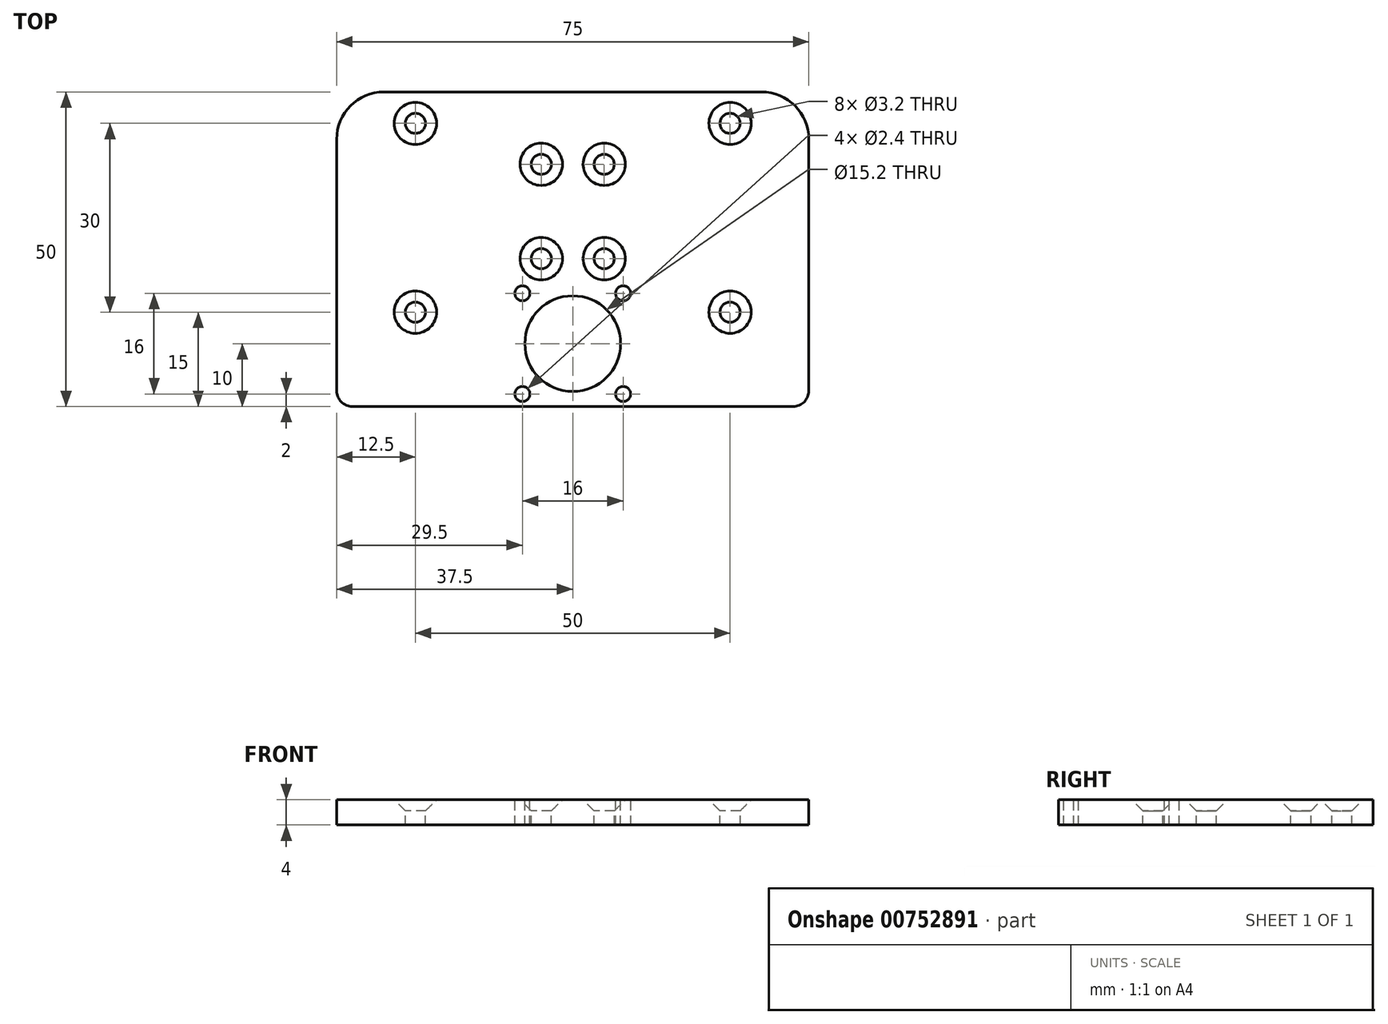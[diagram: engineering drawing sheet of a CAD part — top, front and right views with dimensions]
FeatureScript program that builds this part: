
annotation { "Feature Type Name" : "Feature", "Feature Type Description" : "" }
export const myFeature = defineFeature(function(context is Context, id is Id, definition is map)
    precondition{}
    {
        {
            var Q0;
            Q0=qCreatedBy(makeId("Top.planeOp"),FACE);
            var sketch = newSketch(context, id + "F0", { "sketchPlane" : qUnion([Q0])});
            skLineSegment(sketch, "E0.bottom", {"start": v(-10, 10) * mm, "end": v(10, 10) * mm, "construction": true});
            skLineSegment(sketch, "E0.top", {"start": v(-10, -10) * mm, "end": v(10, -10) * mm, "construction": true});
            skLineSegment(sketch, "E0.left", {"start": v(-10, 10) * mm, "end": v(-10, -10) * mm, "construction": true});
            skLineSegment(sketch, "E0.right", {"start": v(10, 10) * mm, "end": v(10, -10) * mm, "construction": true});
            skPoint(sketch, "E0.middle", {"position": v(0, 0) * mm});
            skLineSegment(sketch, "E1.bottom", {"start": v(-8, 8) * mm, "end": v(8, 8) * mm, "construction": true});
            skLineSegment(sketch, "E1.top", {"start": v(-8, -8) * mm, "end": v(8, -8) * mm, "construction": true});
            skLineSegment(sketch, "E1.left", {"start": v(-8, 8) * mm, "end": v(-8, -8) * mm, "construction": true});
            skLineSegment(sketch, "E1.right", {"start": v(8, 8) * mm, "end": v(8, -8) * mm, "construction": true});
            skPoint(sketch, "E2", {"position": v(-8, 8) * mm});
            skPoint(sketch, "E3", {"position": v(8, 8) * mm});
            skPoint(sketch, "E4", {"position": v(8, -8) * mm});
            skPoint(sketch, "E5", {"position": v(-8, -8) * mm});
            skCircle(sketch, "E6", {"center": v(0, 0) * mm, "radius": 7.6 * mm});
            skLineSegment(sketch, "E7.bottom", {"start": v(-20, 0) * mm, "end": v(-30, 0) * mm, "construction": true});
            skLineSegment(sketch, "E7.top", {"start": v(-20, 10) * mm, "end": v(-30, 10) * mm, "construction": true});
            skLineSegment(sketch, "E7.left", {"start": v(-20, 0) * mm, "end": v(-20, 10) * mm, "construction": true});
            skLineSegment(sketch, "E7.right", {"start": v(-30, 0) * mm, "end": v(-30, 10) * mm, "construction": true});
            skPoint(sketch, "E7.middle", {"position": v(-25, 5) * mm});
            skLineSegment(sketch, "E8.bottom", {"start": v(-20, -6.5) * mm, "end": v(-30, -6.5) * mm, "construction": true});
            skLineSegment(sketch, "E8.left", {"start": v(-20, -6.5) * mm, "end": v(-20, 0) * mm, "construction": true});
            skLineSegment(sketch, "E8.right", {"start": v(-30, -6.5) * mm, "end": v(-30, 0) * mm, "construction": true});
            skLineSegment(sketch, "E9.bottom", {"start": v(-35, -2) * mm, "end": v(-30, -2) * mm, "construction": true});
            skLineSegment(sketch, "E9.top", {"start": v(-35, -10) * mm, "end": v(-15, -10) * mm, "construction": true});
            skLineSegment(sketch, "E9.left", {"start": v(-35, -2) * mm, "end": v(-35, -10) * mm, "construction": true});
            skLineSegment(sketch, "E9.right", {"start": v(-15, -2) * mm, "end": v(-15, -10) * mm, "construction": true});
            skCircle(sketch, "E10.0", {"center": v(0, 0) * mm, "radius": 3 * mm, "construction": true});
            skLineSegment(sketch, "E11.MirrorCS", {"start": v(20, 10) * mm, "end": v(30, 10) * mm, "construction": true});
            skLineSegment(sketch, "E12.MirrorCS", {"start": v(30, 0) * mm, "end": v(30, 10) * mm, "construction": true});
            skLineSegment(sketch, "E13.MirrorCS", {"start": v(20, 0) * mm, "end": v(20, 10) * mm, "construction": true});
            skPoint(sketch, "E14.MirrorP", {"position": v(25, 5) * mm});
            skLineSegment(sketch, "E15.MirrorCS", {"start": v(20, 0) * mm, "end": v(30, 0) * mm, "construction": true});
            skLineSegment(sketch, "E16.MirrorCS", {"start": v(30, -6.5) * mm, "end": v(30, 0) * mm, "construction": true});
            skLineSegment(sketch, "E17.MirrorCS", {"start": v(20, -6.5) * mm, "end": v(20, 0) * mm, "construction": true});
            skLineSegment(sketch, "E18.MirrorCS", {"start": v(35, -2) * mm, "end": v(15, -2) * mm, "construction": true});
            skLineSegment(sketch, "E19.MirrorCS", {"start": v(35, -2) * mm, "end": v(35, -10) * mm, "construction": true});
            skLineSegment(sketch, "E20.MirrorCS", {"start": v(15, -2) * mm, "end": v(15, -10) * mm, "construction": true});
            skLineSegment(sketch, "E21.MirrorCS", {"start": v(20, -6.5) * mm, "end": v(30, -6.5) * mm, "construction": true});
            skLineSegment(sketch, "E22.MirrorCS", {"start": v(35, -10) * mm, "end": v(15, -10) * mm, "construction": true});
            skLineSegment(sketch, "E23.trimOffspring", {"start": v(-20, -2) * mm, "end": v(-15, -2) * mm, "construction": true});
            skLineSegment(sketch, "E24.bottom", {"start": v(-37.5, 40) * mm, "end": v(37.5, 40) * mm});
            skLineSegment(sketch, "E24.top", {"start": v(-37.5, -10) * mm, "end": v(37.5, -10) * mm});
            skLineSegment(sketch, "E24.right", {"start": v(37.5, 40) * mm, "end": v(37.5, -10) * mm});
            skLineSegment(sketch, "E25.bottom", {"start": v(-14.45, 31) * mm, "end": v(14.45, 31) * mm, "construction": true});
            skLineSegment(sketch, "E25.top", {"start": v(-14.45, 11) * mm, "end": v(14.45, 11) * mm, "construction": true});
            skLineSegment(sketch, "E25.left", {"start": v(-14.45, 31) * mm, "end": v(-14.45, 11) * mm, "construction": true});
            skLineSegment(sketch, "E25.right", {"start": v(14.45, 31) * mm, "end": v(14.45, 11) * mm, "construction": true});
            skPoint(sketch, "E25.middle", {"position": v(0, 21) * mm});
            skLineSegment(sketch, "E26.bottom", {"start": v(-5, 28.5) * mm, "end": v(5, 28.5) * mm, "construction": true});
            skLineSegment(sketch, "E26.top", {"start": v(-5, 13.5) * mm, "end": v(5, 13.5) * mm, "construction": true});
            skLineSegment(sketch, "E26.left", {"start": v(-5, 28.5) * mm, "end": v(-5, 13.5) * mm, "construction": true});
            skLineSegment(sketch, "E26.right", {"start": v(5, 28.5) * mm, "end": v(5, 13.5) * mm, "construction": true});
            skLineSegment(sketch, "E27.bottom", {"start": v(37.5, 26) * mm, "end": v(-37.5, 26) * mm, "construction": true});
            skLineSegment(sketch, "E27.top", {"start": v(37.5, 16) * mm, "end": v(-37.5, 16) * mm, "construction": true});
            skLineSegment(sketch, "E27.left", {"start": v(37.5, 26) * mm, "end": v(37.5, 16) * mm, "construction": true});
            skLineSegment(sketch, "E27.right", {"start": v(-37.5, 26) * mm, "end": v(-37.5, 16) * mm, "construction": true});
            skLineSegment(sketch, "E28", {"start": v(-37.5, 21) * mm, "end": v(37.5, 21) * mm, "construction": true});
            skLineSegment(sketch, "E29", {"start": v(-37.5, 40) * mm, "end": v(-37.5, -10) * mm});
            skLineSegment(sketch, "E30.bottom", {"start": v(12.5, 5) * mm, "end": v(-12.5, 5) * mm, "construction": true});
            skLineSegment(sketch, "E30.top", {"start": v(12.5, -5) * mm, "end": v(-12.5, -5) * mm, "construction": true});
            skLineSegment(sketch, "E30.left", {"start": v(12.5, 5) * mm, "end": v(12.5, -5) * mm, "construction": true});
            skLineSegment(sketch, "E30.right", {"start": v(-12.5, 5) * mm, "end": v(-12.5, -5) * mm, "construction": true});
            skLineSegment(sketch, "E31.bottom", {"start": v(-30, 40) * mm, "end": v(-20, 40) * mm, "construction": true});
            skLineSegment(sketch, "E31.top", {"start": v(-30, 30) * mm, "end": v(-20, 30) * mm, "construction": true});
            skLineSegment(sketch, "E31.left", {"start": v(-30, 40) * mm, "end": v(-30, 30) * mm, "construction": true});
            skLineSegment(sketch, "E31.right", {"start": v(-20, 40) * mm, "end": v(-20, 30) * mm, "construction": true});
            skPoint(sketch, "E31.middle", {"position": v(-25, 35) * mm});
            skLineSegment(sketch, "E32.MirrorCS", {"start": v(20, 40) * mm, "end": v(20, 30) * mm, "construction": true});
            skLineSegment(sketch, "E33.MirrorCS", {"start": v(30, 40) * mm, "end": v(20, 40) * mm, "construction": true});
            skLineSegment(sketch, "E34.MirrorCS", {"start": v(30, 40) * mm, "end": v(30, 30) * mm, "construction": true});
            skLineSegment(sketch, "E35.MirrorCS", {"start": v(30, 30) * mm, "end": v(20, 30) * mm, "construction": true});
            skPoint(sketch, "E36.MirrorP", {"position": v(25, 35) * mm});
            skCircle(sketch, "E37", {"center": v(-5, 13.5) * mm, "radius": 3 * mm, "construction": true});
            skSolve(sketch);
        }
        {
            var Q0;
            Q0=makeQuery(id+"F0.imprint","IMPRINT",FACE,{"disambiguationData":[TD([[makeQuery(id+"F0.imprint","IMPRINT",EDGE,{"derivedFrom":sQuery(id+"F0.wireOp",EDGE,"E6")}),-1.0]])]});
            extrude(context, id + "F1", {"entities" : qUnion([Q0]), "oppositeDirection" : true, "depth" : 4 * mm, "offsetDistance" : 25 * mm});
        }
        {
            var Q0;
            Q0=sQuery(id+"F0.wireOp",VERTEX,"E2");
            var Q1;
            Q1=sQuery(id+"F0.wireOp",VERTEX,"E3");
            var Q2;
            Q2=sQuery(id+"F0.wireOp",VERTEX,"E4");
            var Q3;
            Q3=sQuery(id+"F0.wireOp",VERTEX,"E5");
            var Q4;
            Q4=makeQuery(id+"F1.opExtrude","SWEPT_BODY",BODY,{"disambiguationData":[OSD([sQuery(id+"F0.wireOp",EDGE,"E6"),sQuery(id+"F0.wireOp",EDGE,"E24.bottom"),sQuery(id+"F0.wireOp",EDGE,"E24.top"),sQuery(id+"F0.wireOp",EDGE,"E24.left"),sQuery(id+"F0.wireOp",EDGE,"E24.right")])]});
            hole(context, id + "F2", {"style" : HoleStyle.SIMPLE, "endStyle" : HoleEndStyle.THROUGH, "standardTappedOrClearance" : lookupTablePath({ "fit" : "Normal", "standard" : "ISO", "size" : "M2", "type" : "Clearance" }), "standardBlindInLast" : lookupTablePath({ "fit" : "Normal", "standard" : "ISO", "engagement" : "75%", "pitch" : "0.25 mm", "size" : "M2", "type" : "Clearance & tapped" }), "holeDiameter" : 2.4 * mm, "majorDiameter" : 2 * mm, "isTappedThrough" : true, "tappedDepth" : 3 * mm, "tapClearance" : 3, "startFromSketch" : true, "locations" : qUnion([Q0, Q1, Q2, Q3]), "scope" : qUnion([Q4])});
        }
        {
            var Q0;
            Q0=sQuery(id+"F0.wireOp",VERTEX,"E7.middle");
            var Q1;
            Q1=sQuery(id+"F0.wireOp",VERTEX,"E14.MirrorP");
            var Q2;
            Q2=sQuery(id+"F0.wireOp",VERTEX,"379273be-aec1-4a05-9cb9-dedefb76e79c0.MirrorP");
            var Q3;
            Q3=sQuery(id+"F0.wireOp",VERTEX,"66311432-f337-42e8-b5ac-b30e00d571a50.MirrorP");
            var Q4;
            Q4=sQuery(id+"F0.wireOp",VERTEX,"E26.bottom.start");
            var Q5;
            Q5=sQuery(id+"F0.wireOp",VERTEX,"E26.bottom.end");
            var Q6;
            Q6=sQuery(id+"F0.wireOp",VERTEX,"E26.top.end");
            var Q7;
            Q7=sQuery(id+"F0.wireOp",VERTEX,"E26.top.start");
            var Q8;
            Q8=sQuery(id+"F0.wireOp",VERTEX,"E31.middle");
            var Q9;
            Q9=sQuery(id+"F0.wireOp",VERTEX,"E36.MirrorP");
            var Q10;
            Q10=makeQuery(id+"F1.opExtrude","SWEPT_BODY",BODY,{"disambiguationData":[OSD([sQuery(id+"F0.wireOp",EDGE,"E6"),sQuery(id+"F0.wireOp",EDGE,"E24.bottom"),sQuery(id+"F0.wireOp",EDGE,"E24.top"),sQuery(id+"F0.wireOp",EDGE,"E24.left"),sQuery(id+"F0.wireOp",EDGE,"E24.right")])]});
            hole(context, id + "F3", {"style" : HoleStyle.C_SINK, "endStyle" : HoleEndStyle.THROUGH, "standardTappedOrClearance" : lookupTablePath({ "fit" : "Close", "standard" : "ISO", "size" : "M3", "type" : "Clearance" }), "standardBlindInLast" : lookupTablePath({ "fit" : "Close", "standard" : "ISO", "engagement" : "75%", "pitch" : "0.5 mm", "size" : "M3", "type" : "Clearance & tapped" }), "holeDiameter" : 3.2 * mm, "cSinkDiameter" : 6.72 * mm, "cSinkAngle" : 90 * degree, "majorDiameter" : 5 * mm, "isTappedThrough" : true, "tappedDepth" : 3 * mm, "tapClearance" : 3, "startFromSketch" : true, "locations" : qUnion([Q0, Q1, Q2, Q3, Q4, Q5, Q6, Q7, Q8, Q9]), "scope" : qUnion([Q10])});
        }
        {
            var Q0;
            Q0=makeQuery(id+"F1.opExtrude","SWEPT_EDGE",EDGE,{"disambiguationData":[OSD([sQuery(id+"F0.wireOp",EDGE,"E24.bottom"),sQuery(id+"F0.wireOp",EDGE,"E29")])]});
            var Q1;
            Q1=makeQuery(id+"F1.opExtrude","SWEPT_EDGE",EDGE,{"disambiguationData":[OSD([sQuery(id+"F0.wireOp",EDGE,"E24.bottom"),sQuery(id+"F0.wireOp",EDGE,"E24.right")])]});
            fillet(context, id + "F4", {"entities" : qUnion([Q0, Q1]), "tangentPropagation" : true, "radius" : 7.5 * mm, "defaultsChanged" : false, "vertexSettings" : [], "allowEdgeOverflow" : false});
        }
        {
            var Q0;
            Q0=makeQuery(id+"F1.opExtrude","SWEPT_EDGE",EDGE,{"disambiguationData":[OSD([sQuery(id+"F0.wireOp",EDGE,"E24.top"),sQuery(id+"F0.wireOp",EDGE,"E29")])]});
            var Q1;
            Q1=makeQuery(id+"F1.opExtrude","SWEPT_EDGE",EDGE,{"disambiguationData":[OSD([sQuery(id+"F0.wireOp",EDGE,"E24.top"),sQuery(id+"F0.wireOp",EDGE,"E24.right")])]});
            fillet(context, id + "F5", {"entities" : qUnion([Q0, Q1]), "tangentPropagation" : true, "radius" : 2.5 * mm, "defaultsChanged" : true, "vertexSettings" : [], "allowEdgeOverflow" : false});
        }
    });
